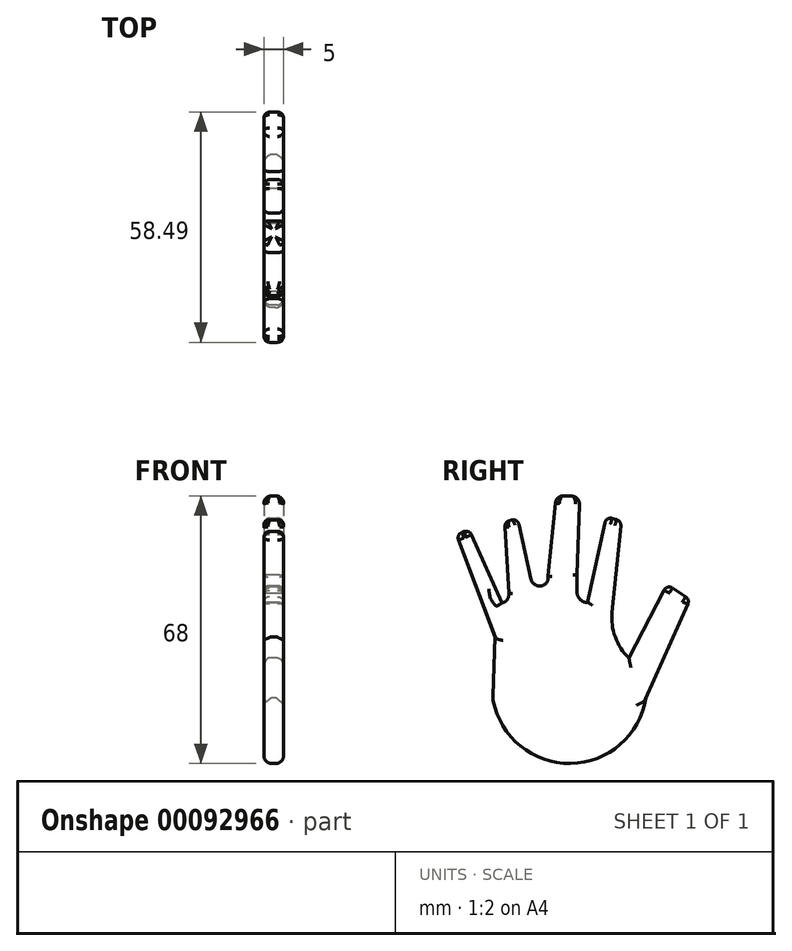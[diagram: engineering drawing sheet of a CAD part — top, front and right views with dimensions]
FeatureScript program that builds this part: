
annotation { "Feature Type Name" : "Feature", "Feature Type Description" : "" }
export const myFeature = defineFeature(function(context is Context, id is Id, definition is map)
    precondition{}
    {
        {
            var Q0;
            Q0=qCreatedBy(makeId("Right.planeOp"),FACE);
            var sketch = newSketch(context, id + "F0", { "sketchPlane" : qUnion([Q0])});
            skLineSegment(sketch, "E0", {"start": v(-19.98, 0) * mm, "end": v(-19.37, 15.61) * mm});
            skLineSegment(sketch, "E1", {"start": v(-19.37, 15.61) * mm, "end": v(-29.22, 41.58) * mm});
            skLineSegment(sketch, "E2", {"start": v(-29.22, 41.58) * mm, "end": v(-25.98, 42.8) * mm});
            skLineSegment(sketch, "E3", {"start": v(-3.87, 51.46) * mm, "end": v(2.1, 51.25) * mm});
            skLineSegment(sketch, "E4", {"start": v(8.8, 46.09) * mm, "end": v(12.68, 45.01) * mm});
            skLineSegment(sketch, "E5", {"start": v(12.68, 45.01) * mm, "end": v(10.31, 21.8) * mm});
            skArc(sketch, "E6", {"start": v(10.31, 21.8) * mm, "mid": v(11.12, 15.5) * mm, "end": v(14.61, 10.2) * mm});
            skLineSegment(sketch, "E7", {"start": v(14.61, 10.2) * mm, "end": v(24.28, 28.9) * mm});
            skLineSegment(sketch, "E8", {"start": v(24.28, 28.9) * mm, "end": v(30.08, 25.03) * mm});
            skLineSegment(sketch, "E9", {"start": v(30.08, 25.03) * mm, "end": v(18.9, 0) * mm});
            skLineSegment(sketch, "E10", {"start": v(-25.98, 42.8) * mm, "end": v(-17.7, 24.17) * mm});
            skLineSegment(sketch, "E11", {"start": v(2.1, 51.25) * mm, "end": v(1.4, 31.32) * mm});
            skLineSegment(sketch, "E12", {"start": v(-3.87, 51.46) * mm, "end": v(-5.94, 30.94) * mm});
            skLineSegment(sketch, "E13", {"start": v(8.8, 46.09) * mm, "end": v(4.03, 24.3) * mm});
            skLineSegment(sketch, "E14", {"start": v(1.4, 31.32) * mm, "end": v(1.4, 26.98) * mm});
            skLineSegment(sketch, "E15", {"start": v(-13.7, 45.74) * mm, "end": v(-16.95, 44.72) * mm});
            skLineSegment(sketch, "E16", {"start": v(-16.95, 44.72) * mm, "end": v(-15.94, 26.6) * mm});
            skLineSegment(sketch, "E17", {"start": v(-13.7, 45.74) * mm, "end": v(-10.23, 30.16) * mm});
            skArc(sketch, "E18", {"start": v(-17.7, 24.17) * mm, "mid": v(-16.32, 25.03) * mm, "end": v(-15.94, 26.6) * mm});
            skArc(sketch, "E19", {"start": v(-10.23, 30.16) * mm, "mid": v(-7.72, 28.49) * mm, "end": v(-5.94, 30.94) * mm});
            skArc(sketch, "E20", {"start": v(1.4, 26.98) * mm, "mid": v(2.17, 25.1) * mm, "end": v(4.03, 24.3) * mm});
            skArc(sketch, "E21", {"start": v(-19.98, 0) * mm, "mid": v(-0.54, -16.6) * mm, "end": v(18.9, 0) * mm});
            skSolve(sketch);
        }
        {
            var Q0;
            Q0 = qSketchRegion(id + "F0", true);
            extrude(context, id + "F1", {"entities" : qUnion([Q0]), "depth" : 5 * mm});
        }
        {
            var Q0;
            Q0=makeQuery(id+"F1.opExtrude","SWEPT_EDGE",EDGE,{"disambiguationData":[OSD([sQuery(id+"F0.wireOp",EDGE,"E2"),sQuery(id+"F0.wireOp",EDGE,"OsZYuTLG-rtLN-KPkL-f2ni-qejcdTJcd4nT")])]});
            var Q1;
            Q1=makeQuery(id+"F1.opExtrude","CAP_EDGE",EDGE,{"disambiguationData":[OSD([sQuery(id+"F0.wireOp",EDGE,"E2")])],"isStart":false});
            var Q2;
            Q2=makeQuery(id+"F1.opExtrude","SWEPT_EDGE",EDGE,{"disambiguationData":[OSD([sQuery(id+"F0.wireOp",EDGE,"E1"),sQuery(id+"F0.wireOp",EDGE,"E2")])]});
            var Q3;
            Q3=makeQuery(id+"F1.opExtrude","CAP_EDGE",EDGE,{"disambiguationData":[OSD([sQuery(id+"F0.wireOp",EDGE,"E2")])],"isStart":true});
            fillet(context, id + "F2", {"entities" : qUnion([Q0, Q1, Q2, Q3]), "radius" : 1.5 * mm, "tangentPropagation" : true, "allowEdgeOverflow" : false});
        }
        {
            var Q0;
            Q0=makeQuery(id+"F1.opExtrude","SWEPT_EDGE",EDGE,{"disambiguationData":[OSD([sQuery(id+"F0.wireOp",EDGE,"xfCbk0J1-wF84-dSMK-NDVN-bKG4vfOAiJcW"),sQuery(id+"F0.wireOp",EDGE,"E3")])]});
            var Q1;
            Q1=makeQuery(id+"F1.opExtrude","CAP_EDGE",EDGE,{"disambiguationData":[OSD([sQuery(id+"F0.wireOp",EDGE,"E3")])],"isStart":true});
            var Q2;
            Q2=makeQuery(id+"F1.opExtrude","SWEPT_EDGE",EDGE,{"disambiguationData":[OSD([sQuery(id+"F0.wireOp",EDGE,"E3"),sQuery(id+"F0.wireOp",EDGE,"uwZNWdPC-O7J5-yE9s-DsNM-UMIqnyBpJ44T")])]});
            var Q3;
            Q3=makeQuery(id+"F1.opExtrude","CAP_EDGE",EDGE,{"disambiguationData":[OSD([sQuery(id+"F0.wireOp",EDGE,"E3")])],"isStart":false});
            fillet(context, id + "F3", {"entities" : qUnion([Q0, Q1, Q2, Q3]), "radius" : 2 * mm, "tangentPropagation" : true, "allowEdgeOverflow" : false});
        }
        {
            var Q0;
            Q0=makeQuery(id+"F1.opExtrude","CAP_EDGE",EDGE,{"disambiguationData":[OSD([sQuery(id+"F0.wireOp",EDGE,"E10")])],"isStart":true});
            var Q1;
            Q1=makeQuery(id+"F1.opExtrude","CAP_EDGE",EDGE,{"disambiguationData":[OSD([sQuery(id+"F0.wireOp",EDGE,"E10")])],"isStart":false});
            var Q2;
            Q2=makeQuery(id+"F1.opExtrude","CAP_EDGE",EDGE,{"disambiguationData":[OSD([sQuery(id+"F0.wireOp",EDGE,"E1")])],"isStart":false});
            var Q3;
            Q3=makeQuery(id+"F1.opExtrude","CAP_EDGE",EDGE,{"disambiguationData":[OSD([sQuery(id+"F0.wireOp",EDGE,"E1")])],"isStart":true});
            fillet(context, id + "F4", {"entities" : qUnion([Q0, Q1, Q2, Q3]), "radius" : 1.5 * mm, "tangentPropagation" : true, "allowEdgeOverflow" : false});
        }
        {
            var Q0;
            Q0=makeQuery(id+"F1.opExtrude","CAP_EDGE",EDGE,{"disambiguationData":[OSD([sQuery(id+"F0.wireOp",EDGE,"E15")])],"isStart":false});
            var Q1;
            Q1=makeQuery(id+"F1.opExtrude","SWEPT_EDGE",EDGE,{"disambiguationData":[OSD([sQuery(id+"F0.wireOp",EDGE,"E15"),sQuery(id+"F0.wireOp",EDGE,"E17")])]});
            var Q2;
            Q2=makeQuery(id+"F1.opExtrude","CAP_EDGE",EDGE,{"disambiguationData":[OSD([sQuery(id+"F0.wireOp",EDGE,"E15")])],"isStart":true});
            var Q3;
            Q3=makeQuery(id+"F1.opExtrude","SWEPT_EDGE",EDGE,{"disambiguationData":[OSD([sQuery(id+"F0.wireOp",EDGE,"E15"),sQuery(id+"F0.wireOp",EDGE,"E16")])]});
            fillet(context, id + "F5", {"entities" : qUnion([Q0, Q1, Q2, Q3]), "radius" : 1.5 * mm, "tangentPropagation" : true, "allowEdgeOverflow" : false});
        }
        {
            var Q0;
            Q0=makeQuery(id+"F1.opExtrude","CAP_EDGE",EDGE,{"disambiguationData":[OSD([sQuery(id+"F0.wireOp",EDGE,"E16")])],"isStart":false});
            var Q1;
            Q1=makeQuery(id+"F1.opExtrude","CAP_EDGE",EDGE,{"disambiguationData":[OSD([sQuery(id+"F0.wireOp",EDGE,"E17")])],"isStart":false});
            var Q2;
            Q2=makeQuery(id+"F1.opExtrude","CAP_EDGE",EDGE,{"disambiguationData":[OSD([sQuery(id+"F0.wireOp",EDGE,"E17")])],"isStart":true});
            var Q3;
            Q3=makeQuery(id+"F1.opExtrude","CAP_EDGE",EDGE,{"disambiguationData":[OSD([sQuery(id+"F0.wireOp",EDGE,"E16")])],"isStart":true});
            fillet(context, id + "F6", {"entities" : qUnion([Q0, Q1, Q2, Q3]), "radius" : 1 * mm, "tangentPropagation" : true, "allowEdgeOverflow" : false});
        }
        {
            var Q0;
            Q0=makeQuery(id+"F1.opExtrude","CAP_EDGE",EDGE,{"disambiguationData":[OSD([sQuery(id+"F0.wireOp",EDGE,"E12")])],"isStart":false});
            var Q1;
            Q1=makeQuery(id+"F1.opExtrude","CAP_EDGE",EDGE,{"disambiguationData":[OSD([sQuery(id+"F0.wireOp",EDGE,"E12")])],"isStart":true});
            var Q2;
            Q2=makeQuery(id+"F1.opExtrude","CAP_EDGE",EDGE,{"disambiguationData":[OSD([sQuery(id+"F0.wireOp",EDGE,"E11")])],"isStart":false});
            var Q3;
            Q3=makeQuery(id+"F1.opExtrude","CAP_EDGE",EDGE,{"disambiguationData":[OSD([sQuery(id+"F0.wireOp",EDGE,"E11")])],"isStart":true});
            fillet(context, id + "F7", {"entities" : qUnion([Q0, Q1, Q2, Q3]), "radius" : 1 * mm, "tangentPropagation" : true, "allowEdgeOverflow" : false});
        }
        {
            var Q0;
            Q0=makeQuery(id+"F1.opExtrude","CAP_EDGE",EDGE,{"disambiguationData":[OSD([sQuery(id+"F0.wireOp",EDGE,"E4")])],"isStart":true});
            var Q1;
            Q1=makeQuery(id+"F1.opExtrude","SWEPT_EDGE",EDGE,{"disambiguationData":[OSD([sQuery(id+"F0.wireOp",EDGE,"E4"),sQuery(id+"F0.wireOp",EDGE,"E5")])]});
            var Q2;
            Q2=makeQuery(id+"F1.opExtrude","CAP_EDGE",EDGE,{"disambiguationData":[OSD([sQuery(id+"F0.wireOp",EDGE,"E4")])],"isStart":false});
            var Q3;
            Q3=makeQuery(id+"F1.opExtrude","SWEPT_EDGE",EDGE,{"disambiguationData":[OSD([sQuery(id+"F0.wireOp",EDGE,"E4"),sQuery(id+"F0.wireOp",EDGE,"E13")])]});
            fillet(context, id + "F8", {"entities" : qUnion([Q0, Q1, Q2, Q3]), "radius" : 1.5 * mm, "tangentPropagation" : true, "allowEdgeOverflow" : false});
        }
        {
            var Q0;
            Q0=makeQuery(id+"F1.opExtrude","CAP_EDGE",EDGE,{"disambiguationData":[OSD([sQuery(id+"F0.wireOp",EDGE,"E5")])],"isStart":true});
            var Q1;
            Q1=makeQuery(id+"F1.opExtrude","CAP_EDGE",EDGE,{"disambiguationData":[OSD([sQuery(id+"F0.wireOp",EDGE,"E5")])],"isStart":false});
            var Q2;
            Q2=makeQuery(id+"F1.opExtrude","CAP_EDGE",EDGE,{"disambiguationData":[OSD([sQuery(id+"F0.wireOp",EDGE,"E13")])],"isStart":true});
            var Q3;
            Q3=makeQuery(id+"F1.opExtrude","CAP_EDGE",EDGE,{"disambiguationData":[OSD([sQuery(id+"F0.wireOp",EDGE,"E13")])],"isStart":false});
            fillet(context, id + "F9", {"entities" : qUnion([Q0, Q1, Q2, Q3]), "radius" : 1.5 * mm, "tangentPropagation" : true, "allowEdgeOverflow" : false});
        }
        {
            var Q0;
            Q0=makeQuery(id+"F1.opExtrude","CAP_EDGE",EDGE,{"disambiguationData":[OSD([sQuery(id+"F0.wireOp",EDGE,"E8")])],"isStart":true});
            var Q1;
            Q1=makeQuery(id+"F1.opExtrude","CAP_EDGE",EDGE,{"disambiguationData":[OSD([sQuery(id+"F0.wireOp",EDGE,"E8")])],"isStart":false});
            var Q2;
            Q2=makeQuery(id+"F1.opExtrude","SWEPT_EDGE",EDGE,{"disambiguationData":[OSD([sQuery(id+"F0.wireOp",EDGE,"E8"),sQuery(id+"F0.wireOp",EDGE,"E9")])]});
            var Q3;
            Q3=makeQuery(id+"F1.opExtrude","SWEPT_EDGE",EDGE,{"disambiguationData":[OSD([sQuery(id+"F0.wireOp",EDGE,"E7"),sQuery(id+"F0.wireOp",EDGE,"E8")])]});
            fillet(context, id + "F10", {"entities" : qUnion([Q0, Q1, Q2, Q3]), "radius" : 1.5 * mm, "tangentPropagation" : true, "allowEdgeOverflow" : false});
        }
        {
            var Q0;
            Q0=makeQuery(id+"F1.opExtrude","CAP_EDGE",EDGE,{"disambiguationData":[OSD([sQuery(id+"F0.wireOp",EDGE,"E9")])],"isStart":false});
            var Q1;
            Q1=makeQuery(id+"F1.opExtrude","CAP_EDGE",EDGE,{"disambiguationData":[OSD([sQuery(id+"F0.wireOp",EDGE,"E9")])],"isStart":true});
            var Q2;
            Q2=makeQuery(id+"F1.opExtrude","CAP_EDGE",EDGE,{"disambiguationData":[OSD([sQuery(id+"F0.wireOp",EDGE,"E7")])],"isStart":false});
            var Q3;
            Q3=makeQuery(id+"F1.opExtrude","CAP_EDGE",EDGE,{"disambiguationData":[OSD([sQuery(id+"F0.wireOp",EDGE,"E7")])],"isStart":true});
            fillet(context, id + "F11", {"entities" : qUnion([Q0, Q1, Q2, Q3]), "radius" : 1.5 * mm, "tangentPropagation" : true, "allowEdgeOverflow" : false});
        }
        {
            var Q0;
            Q0=makeQuery(id+"F1.opExtrude","SWEPT_EDGE",EDGE,{"disambiguationData":[OSD([sQuery(id+"F0.wireOp",EDGE,"E0"),sQuery(id+"F0.wireOp",EDGE,"E21")])]});
            fillet(context, id + "F12", {"entities" : qUnion([Q0]), "radius" : 5 * mm, "tangentPropagation" : true, "allowEdgeOverflow" : false});
        }
        {
            var Q0;
            Q0=makeQuery(id+"F1.opExtrude","CAP_EDGE",EDGE,{"disambiguationData":[OSD([sQuery(id+"F0.wireOp",EDGE,"E21")])],"isStart":false});
            var Q1;
            Q1=makeQuery(id+"F1.opExtrude","CAP_EDGE",EDGE,{"disambiguationData":[OSD([sQuery(id+"F0.wireOp",EDGE,"E21")])],"isStart":true});
            var Q2;
            {var subQ0=sQuery(id+"F0.wireOp",EDGE,"E21");var subQ1=sQuery(id+"F0.wireOp",EDGE,"E0");Q2=makeQuery(id+"F12.opFillet","BLEND_EDGE",EDGE,{"blendedFrom":[makeQuery(id+"F1.opExtrude","SWEPT_EDGE",EDGE,{"disambiguationData":[OSD([subQ1,subQ0])]}),makeQuery(id+"F1.opExtrude","CAP_FACE",FACE,{"disambiguationData":[OSD([subQ1,sQuery(id+"F0.wireOp",EDGE,"E1"),sQuery(id+"F0.wireOp",EDGE,"E2"),sQuery(id+"F0.wireOp",EDGE,"E3"),sQuery(id+"F0.wireOp",EDGE,"E4"),sQuery(id+"F0.wireOp",EDGE,"E5"),sQuery(id+"F0.wireOp",EDGE,"E6"),sQuery(id+"F0.wireOp",EDGE,"E7"),sQuery(id+"F0.wireOp",EDGE,"E8"),sQuery(id+"F0.wireOp",EDGE,"E9"),sQuery(id+"F0.wireOp",EDGE,"E10"),sQuery(id+"F0.wireOp",EDGE,"E11"),sQuery(id+"F0.wireOp",EDGE,"E12"),sQuery(id+"F0.wireOp",EDGE,"E13"),sQuery(id+"F0.wireOp",EDGE,"E14"),sQuery(id+"F0.wireOp",EDGE,"E15"),sQuery(id+"F0.wireOp",EDGE,"E16"),sQuery(id+"F0.wireOp",EDGE,"E17"),sQuery(id+"F0.wireOp",EDGE,"E18"),sQuery(id+"F0.wireOp",EDGE,"E19"),sQuery(id+"F0.wireOp",EDGE,"E20"),subQ0])],"isStart":true})],"blendedInto":[makeQuery(id+"F1.opExtrude","CAP_FACE",FACE,{"disambiguationData":[OSD([subQ1,sQuery(id+"F0.wireOp",EDGE,"E1"),sQuery(id+"F0.wireOp",EDGE,"E2"),sQuery(id+"F0.wireOp",EDGE,"E3"),sQuery(id+"F0.wireOp",EDGE,"E4"),sQuery(id+"F0.wireOp",EDGE,"E5"),sQuery(id+"F0.wireOp",EDGE,"E6"),sQuery(id+"F0.wireOp",EDGE,"E7"),sQuery(id+"F0.wireOp",EDGE,"E8"),sQuery(id+"F0.wireOp",EDGE,"E9"),sQuery(id+"F0.wireOp",EDGE,"E10"),sQuery(id+"F0.wireOp",EDGE,"E11"),sQuery(id+"F0.wireOp",EDGE,"E12"),sQuery(id+"F0.wireOp",EDGE,"E13"),sQuery(id+"F0.wireOp",EDGE,"E14"),sQuery(id+"F0.wireOp",EDGE,"E15"),sQuery(id+"F0.wireOp",EDGE,"E16"),sQuery(id+"F0.wireOp",EDGE,"E17"),sQuery(id+"F0.wireOp",EDGE,"E18"),sQuery(id+"F0.wireOp",EDGE,"E19"),sQuery(id+"F0.wireOp",EDGE,"E20"),subQ0])],"isStart":true})]});}
            var Q3;
            {var subQ0=sQuery(id+"F0.wireOp",EDGE,"E21");var subQ1=sQuery(id+"F0.wireOp",EDGE,"E0");Q3=makeQuery(id+"F12.opFillet","BLEND_EDGE",EDGE,{"blendedFrom":[makeQuery(id+"F1.opExtrude","SWEPT_EDGE",EDGE,{"disambiguationData":[OSD([subQ1,subQ0])]}),makeQuery(id+"F1.opExtrude","CAP_FACE",FACE,{"disambiguationData":[OSD([subQ1,sQuery(id+"F0.wireOp",EDGE,"E1"),sQuery(id+"F0.wireOp",EDGE,"E2"),sQuery(id+"F0.wireOp",EDGE,"E3"),sQuery(id+"F0.wireOp",EDGE,"E4"),sQuery(id+"F0.wireOp",EDGE,"E5"),sQuery(id+"F0.wireOp",EDGE,"E6"),sQuery(id+"F0.wireOp",EDGE,"E7"),sQuery(id+"F0.wireOp",EDGE,"E8"),sQuery(id+"F0.wireOp",EDGE,"E9"),sQuery(id+"F0.wireOp",EDGE,"E10"),sQuery(id+"F0.wireOp",EDGE,"E11"),sQuery(id+"F0.wireOp",EDGE,"E12"),sQuery(id+"F0.wireOp",EDGE,"E13"),sQuery(id+"F0.wireOp",EDGE,"E14"),sQuery(id+"F0.wireOp",EDGE,"E15"),sQuery(id+"F0.wireOp",EDGE,"E16"),sQuery(id+"F0.wireOp",EDGE,"E17"),sQuery(id+"F0.wireOp",EDGE,"E18"),sQuery(id+"F0.wireOp",EDGE,"E19"),sQuery(id+"F0.wireOp",EDGE,"E20"),subQ0])],"isStart":false})],"blendedInto":[makeQuery(id+"F1.opExtrude","CAP_FACE",FACE,{"disambiguationData":[OSD([subQ1,sQuery(id+"F0.wireOp",EDGE,"E1"),sQuery(id+"F0.wireOp",EDGE,"E2"),sQuery(id+"F0.wireOp",EDGE,"E3"),sQuery(id+"F0.wireOp",EDGE,"E4"),sQuery(id+"F0.wireOp",EDGE,"E5"),sQuery(id+"F0.wireOp",EDGE,"E6"),sQuery(id+"F0.wireOp",EDGE,"E7"),sQuery(id+"F0.wireOp",EDGE,"E8"),sQuery(id+"F0.wireOp",EDGE,"E9"),sQuery(id+"F0.wireOp",EDGE,"E10"),sQuery(id+"F0.wireOp",EDGE,"E11"),sQuery(id+"F0.wireOp",EDGE,"E12"),sQuery(id+"F0.wireOp",EDGE,"E13"),sQuery(id+"F0.wireOp",EDGE,"E14"),sQuery(id+"F0.wireOp",EDGE,"E15"),sQuery(id+"F0.wireOp",EDGE,"E16"),sQuery(id+"F0.wireOp",EDGE,"E17"),sQuery(id+"F0.wireOp",EDGE,"E18"),sQuery(id+"F0.wireOp",EDGE,"E19"),sQuery(id+"F0.wireOp",EDGE,"E20"),subQ0])],"isStart":false})]});}
            var Q4;
            Q4=makeQuery(id+"F1.opExtrude","CAP_EDGE",EDGE,{"disambiguationData":[OSD([sQuery(id+"F0.wireOp",EDGE,"E0")])],"isStart":false});
            var Q5;
            Q5=makeQuery(id+"F1.opExtrude","CAP_EDGE",EDGE,{"disambiguationData":[OSD([sQuery(id+"F0.wireOp",EDGE,"E0")])],"isStart":true});
            fillet(context, id + "F13", {"entities" : qUnion([Q0, Q1, Q2, Q3, Q4, Q5]), "radius" : 2 * mm, "tangentPropagation" : true, "allowEdgeOverflow" : false});
        }
    });
